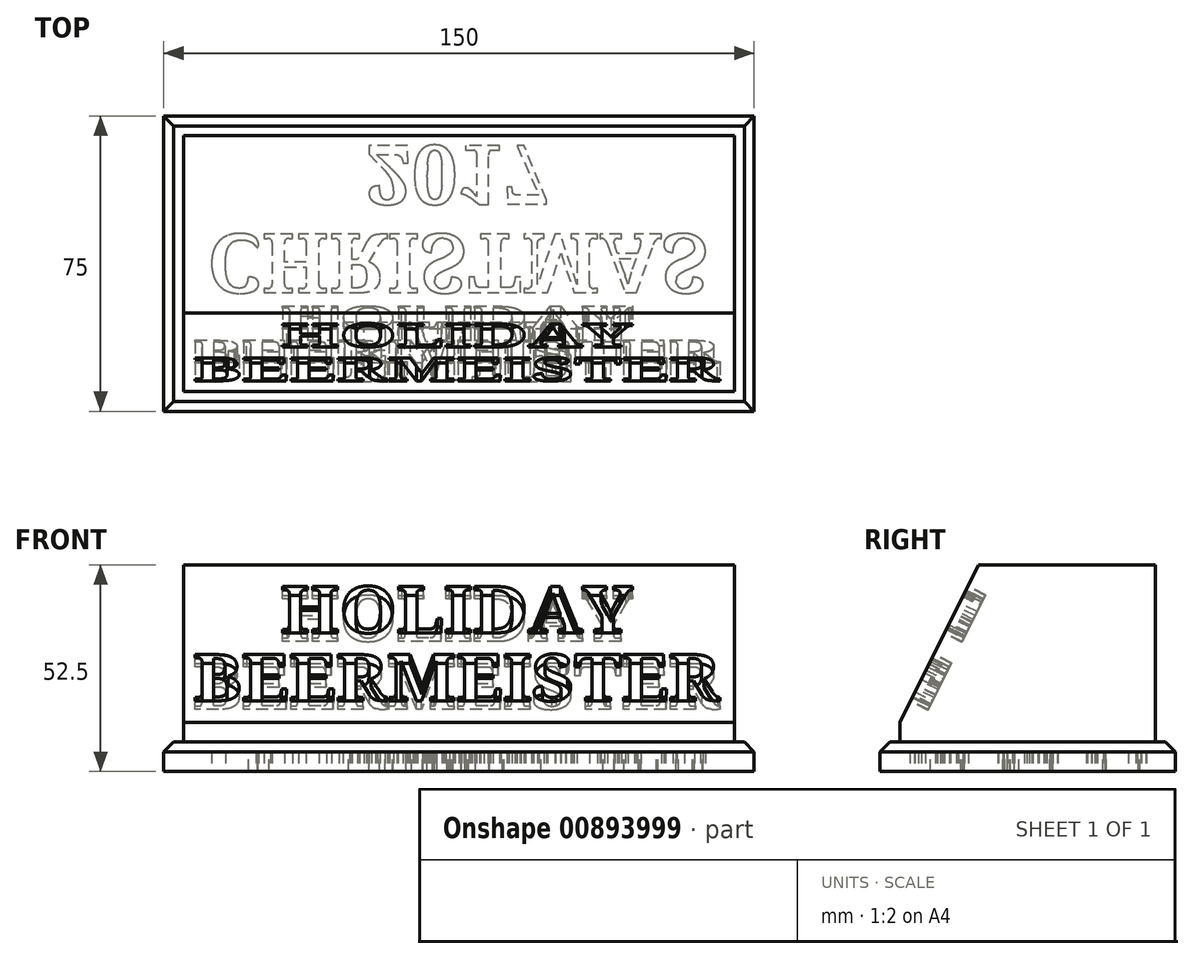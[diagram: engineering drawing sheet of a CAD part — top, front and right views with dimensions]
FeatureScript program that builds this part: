
annotation { "Feature Type Name" : "Feature", "Feature Type Description" : "" }
export const myFeature = defineFeature(function(context is Context, id is Id, definition is map)
    precondition{}
    {
        {
            var Q0;
            Q0=qCreatedBy(makeId("Top.planeOp"),FACE);
            var sketch = newSketch(context, id + "F0", { "sketchPlane" : qUnion([Q0])});
            skLineSegment(sketch, "E0.bottom", {"start": v(75, 37.5) * mm, "end": v(-75, 37.5) * mm});
            skLineSegment(sketch, "E0.top", {"start": v(75, -37.5) * mm, "end": v(-75, -37.5) * mm});
            skLineSegment(sketch, "E0.left", {"start": v(75, 37.5) * mm, "end": v(75, -37.5) * mm});
            skLineSegment(sketch, "E0.right", {"start": v(-75, 37.5) * mm, "end": v(-75, -37.5) * mm});
            skPoint(sketch, "E0.middle", {"position": v(0, 0) * mm});
            skSolve(sketch);
        }
        {
            var Q0;
            Q0 = qSketchRegion(id + "F0", true);
            extrude(context, id + "F1", {"entities" : qUnion([Q0]), "depth" : 7.5 * mm, "offsetDistance" : 25 * mm});
        }
        {
            var Q0;
            Q0=makeQuery(id+"F1.opExtrude","CAP_FACE",FACE,{"disambiguationData":[OSD([sQuery(id+"F0.wireOp",EDGE,"E0.bottom"),sQuery(id+"F0.wireOp",EDGE,"E0.top"),sQuery(id+"F0.wireOp",EDGE,"E0.left"),sQuery(id+"F0.wireOp",EDGE,"E0.right")])],"isStart":false});
            var sketch = newSketch(context, id + "F2", { "sketchPlane" : qUnion([Q0])});
            skLineSegment(sketch, "E1.0", {"start": v(-70, -32.5) * mm, "end": v(70, -32.5) * mm});
            skLineSegment(sketch, "E1.1", {"start": v(-70, 32.5) * mm, "end": v(-70, -32.5) * mm});
            skLineSegment(sketch, "E1.2", {"start": v(70, 32.5) * mm, "end": v(-70, 32.5) * mm});
            skLineSegment(sketch, "E1.3", {"start": v(70, -32.5) * mm, "end": v(70, 32.5) * mm});
            skSolve(sketch);
        }
        {
            var Q0;
            Q0 = qSketchRegion(id + "F2", true);
            extrude(context, id + "F3", {"entities" : qUnion([Q0]), "operationType" : NewBodyOperationType.ADD, "depth" : 45 * mm, "offsetDistance" : 25 * mm});
        }
        {
            var Q0;
            Q0=makeQuery(id+"F3.opExtrude","CAP_EDGE",EDGE,{"disambiguationData":[OSD([sQuery(id+"F2.wireOp",EDGE,"E1.0")])],"isStart":false});
            chamfer(context, id + "F4", {"entities" : qUnion([Q0]), "chamferType" : ChamferType.TWO_OFFSETS, "width1" : 20 * mm, "oppositeDirection" : false, "width2" : 40 * mm, "tangentPropagation" : true});
        }
        {
            var Q0;
            Q0=makeQuery(id+"F1.opExtrude","CAP_EDGE",EDGE,{"disambiguationData":[OSD([sQuery(id+"F0.wireOp",EDGE,"E0.right")])],"isStart":false});
            var Q1;
            Q1=makeQuery(id+"F1.opExtrude","CAP_EDGE",EDGE,{"disambiguationData":[OSD([sQuery(id+"F0.wireOp",EDGE,"E0.top")])],"isStart":false});
            var Q2;
            Q2=makeQuery(id+"F1.opExtrude","CAP_EDGE",EDGE,{"disambiguationData":[OSD([sQuery(id+"F0.wireOp",EDGE,"E0.bottom")])],"isStart":false});
            var Q3;
            Q3=makeQuery(id+"F1.opExtrude","CAP_EDGE",EDGE,{"disambiguationData":[OSD([sQuery(id+"F0.wireOp",EDGE,"E0.left")])],"isStart":false});
            chamfer(context, id + "F5", {"entities" : qUnion([Q0, Q1, Q2, Q3]), "width" : 2.5 * mm, "tangentPropagation" : true});
        }
        {
            var Q0;
            Q0=makeQuery(id+"F4.opChamfer","BLEND_FACE",FACE,{"disambiguationData":[OSD([sQuery(id+"F2.wireOp",EDGE,"E1.0")])]});
            var sketch = newSketch(context, id + "F6", { "sketchPlane" : qUnion([Q0])});
            skText(sketch, "E2", { "text": "HOLIDAY", "fontName": "NotoSerif-Bold.ttf"});
            skPoint(sketch, "E3", {"position": v(0, 41.37) * mm});
            skText(sketch, "E4", { "text": "BEERMEISTER", "fontName": "NotoSerif-Bold.ttf"});
            skLineSegment(sketch, "E5", {"start": v(45.3, 35.27) * mm, "end": v(45.3, 41.37) * mm, "construction": true});
            skLineSegment(sketch, "E6", {"start": v(45.3, 22.06) * mm, "end": v(45.3, 15.96) * mm, "construction": true});
            skLineSegment(sketch, "E7", {"start": v(67.5, 2.75) * mm, "end": v(67.5, -3.35) * mm, "construction": true});
            const initialGuessF6  = {"E2": [-0.0453, 0.02206, 1, 0, 0.01321], "E4": [-0.0675, 0.00275, 1, 0, 0.01321]};
            skSetInitialGuess(sketch, initialGuessF6);
            skSolve(sketch);
        }
        {
            var Q0;
            Q0 = qSketchRegion(id + "F6", true);
            extrude(context, id + "F7", {"entities" : qUnion([Q0]), "operationType" : NewBodyOperationType.REMOVE, "oppositeDirection" : true, "depth" : 5 * mm, "offsetDistance" : 25 * mm});
        }
        {
            var Q0;
            Q0=makeQuery(id+"F1.opExtrude","CAP_FACE",FACE,{"disambiguationData":[OSD([sQuery(id+"F0.wireOp",EDGE,"E0.bottom"),sQuery(id+"F0.wireOp",EDGE,"E0.top"),sQuery(id+"F0.wireOp",EDGE,"E0.left"),sQuery(id+"F0.wireOp",EDGE,"E0.right")])],"isStart":true});
            var sketch = newSketch(context, id + "F8", { "sketchPlane" : qUnion([Q0])});
            skText(sketch, "E8", { "text": "HALF", "fontName": "NotoSerif-Bold.ttf"});
            skText(sketch, "E9", { "text": "CHRISTMAS", "fontName": "NotoSerif-Bold.ttf"});
            skPoint(sketch, "E10", {"position": v(0, 37.5) * mm});
            skPoint(sketch, "E11", {"position": v(-75, 0) * mm});
            skPoint(sketch, "E12", {"position": v(0, 0) * mm});
            skLineSegment(sketch, "E13", {"start": v(-29.97, 15) * mm, "end": v(-29.97, 7.5) * mm, "construction": true});
            skLineSegment(sketch, "E14", {"start": v(-29.97, 30) * mm, "end": v(-29.97, 37.5) * mm, "construction": true});
            skLineSegment(sketch, "E15", {"start": v(-23.62, -15) * mm, "end": v(-23.62, -7.5) * mm, "construction": true});
            skLineSegment(sketch, "E16", {"start": v(-23.62, -30) * mm, "end": v(-23.62, -37.5) * mm, "construction": true});
            skText(sketch, "E17", { "text": "2017", "fontName": "NotoSerif-Bold.ttf"});
            const initialGuessF8  = {"E8": [-0.02997, 0.015, 1, 0, 0.015], "E9": [-0.06396, -0.0075, 1, 0, 0.015], "E17": [-0.02362, -0.03, 1, 0, 0.015]};
            skSetInitialGuess(sketch, initialGuessF8);
            skSolve(sketch);
        }
        {
            var Q0;
            Q0 = qSketchRegion(id + "F8", true);
            extrude(context, id + "F9", {"entities" : qUnion([Q0]), "operationType" : NewBodyOperationType.REMOVE, "oppositeDirection" : true, "depth" : 5 * mm, "offsetDistance" : 25 * mm});
        }
    });
